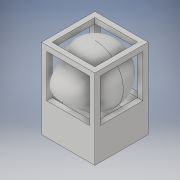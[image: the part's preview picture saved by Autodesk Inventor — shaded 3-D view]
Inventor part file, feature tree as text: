
AUTODESK INVENTOR PART (.ipt)
format: ipt  version: 2019 (Build 230136000, 136)  size: 530,432 bytes
history: native  units: mm
features: sketch x5, extrude x5, plane x1, other x1
ambient origin geometry x8: Origin, YZ Plane, XZ Plane, XY Plane, X Axis, Y Axis, Z Axis, Center Point
bodies: Solid1 (feature_tree), Solid2 (feature_tree)
feature tree (12):
  sketch  "Sketch1"  dims[d0=0.1mm d1=0.1mm]
  extrude  "Extrusion1"  Depth=0.1mm
  extrude  "Extrusion2"  Depth=0.01mm
  extrude  "Extrusion3"  Depth=0.08mm
  extrude  "Extrusion4"  Depth=0.1mm TaperAngle=0.0deg
  plane  "Work Plane1"
  sketch  "Sketch4"  dims[d7=0.08mm d8=0.1mm d9=0.0mm]
  other  "Form1"
  extrude  "Extrusion5"  Depth=0.01mm
  sketch  "Sketch2"  dims[d2=0.1mm d3=0.0mm d4=0.01mm]
  sketch  "Sketch3"  dims[d5=0.01mm d6=0.08mm]
  sketch  "Sketch6"  dims[d10=0.08mm d12=0.01mm d13=0.1mm d14=0.0mm d15=0.01mm d16=0.01mm d17=0.08mm d18=0.08mm d19=0.1mm d20=0.0mm d21=-0.05mm d23=0.02mm d24=0.02mm d25=0.05mm d26=0.0mm]
